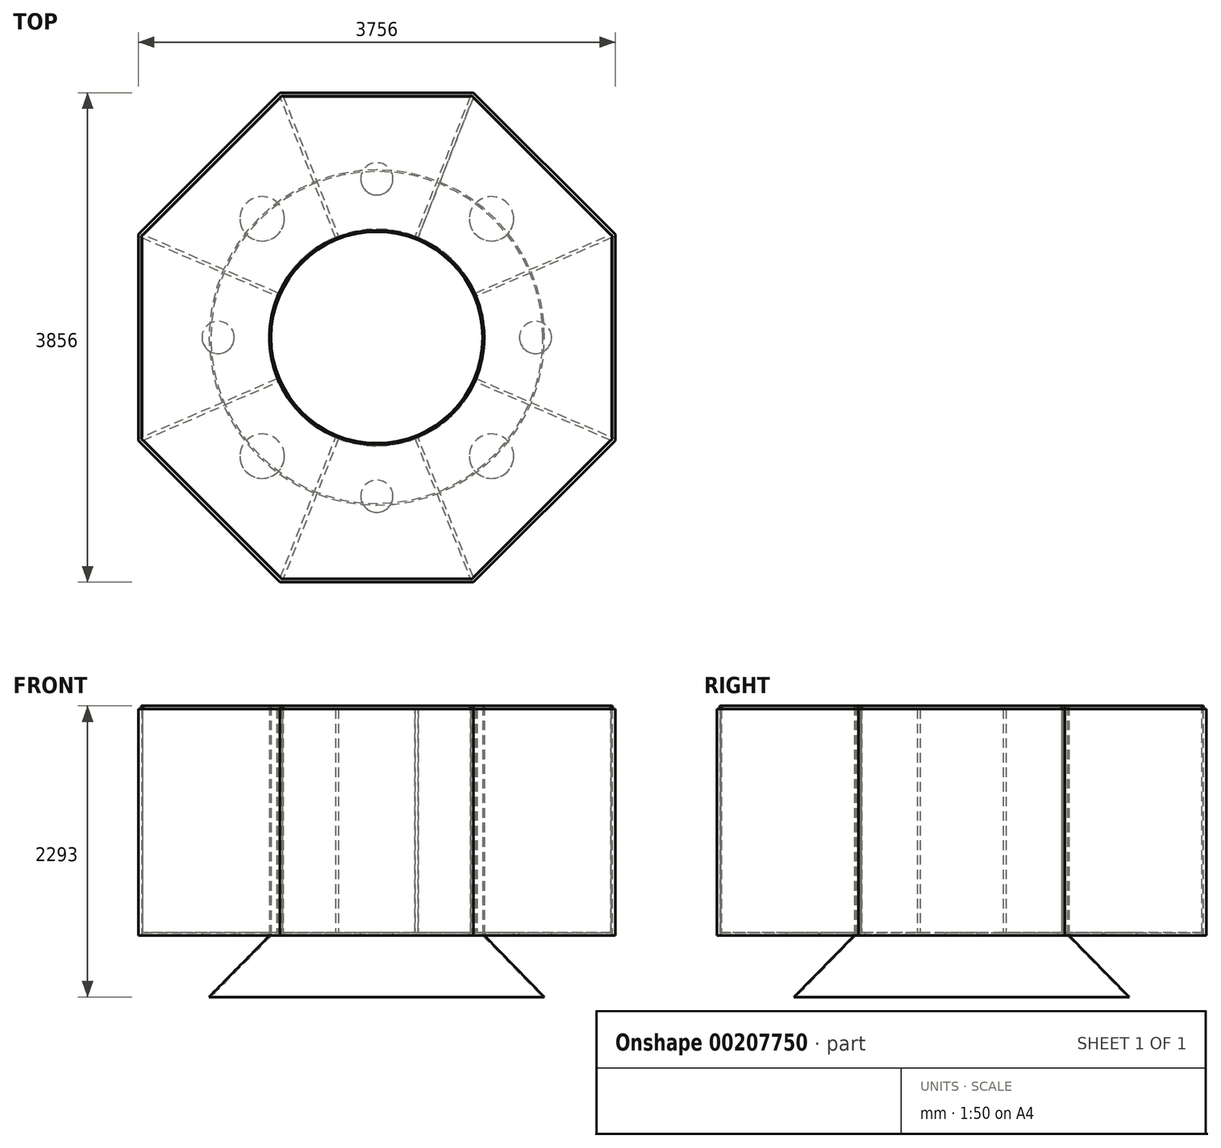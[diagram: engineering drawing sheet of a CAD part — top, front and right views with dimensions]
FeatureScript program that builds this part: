
annotation { "Feature Type Name" : "Feature", "Feature Type Description" : "" }
export const myFeature = defineFeature(function(context is Context, id is Id, definition is map)
    precondition{}
    {
        {
            var Q0;
            Q0=qCreatedBy(makeId("Front.planeOp"),FACE);
            var sketch = newSketch(context, id + "F0", { "sketchPlane" : qUnion([Q0])});
            skLineSegment(sketch, "E0", {"start": v(833, 4071) * mm, "end": v(833, 2261) * mm});
            skLineSegment(sketch, "E1", {"start": v(833, 2261) * mm, "end": v(1308, 1778) * mm});
            skLineSegment(sketch, "E2", {"start": v(1320.7, 1778) * mm, "end": v(845.7, 2261) * mm});
            skLineSegment(sketch, "E3", {"start": v(845.7, 2261) * mm, "end": v(845.7, 4071) * mm});
            skLineSegment(sketch, "E4", {"start": v(845.7, 4071) * mm, "end": v(833, 4071) * mm});
            skLineSegment(sketch, "E5", {"start": v(0, 0) * mm, "end": v(0, 81.95) * mm, "construction": true});
            skLineSegment(sketch, "E6", {"start": v(1308, 1778) * mm, "end": v(1320.7, 1778) * mm});
            skSolve(sketch);
        }
        {
            var Q0;
            Q0 = qSketchRegion(id + "F0", true);
            var Q1;
            Q1=sQuery(id+"F0.wireOp",EDGE,"E5");
            revolve(context, id + "F1", {"surfaceOperationType" : NewSurfaceOperationType.NEW, "entities" : qUnion([Q0]), "axis" : qUnion([Q1]), "revolveType" : RevolveType.FULL});
        }
        {
            var Q0;
            Q0=makeQuery(id+"F1.opRevolve","SWEPT_FACE",FACE,{"disambiguationData":[OSD([sQuery(id+"F0.wireOp",EDGE,"E6")])]});
            cPlane(context, id + "F2", {"entities" : qUnion([Q0]), "cplaneType" : CPlaneType.OFFSET, "offset" : 483 * mm, "oppositeDirection" : true, "width" : 150 * mm, "height" : 150 * mm});
        }
        {
            var Q0;
            Q0=qCreatedBy(id+"F2.planeOp",FACE);
            var sketch = newSketch(context, id + "F3", { "sketchPlane" : qUnion([Q0])});
            skLineSegment(sketch, "E7", {"start": v(-750, -1900) * mm, "end": v(750, -1900) * mm});
            skLineSegment(sketch, "E8", {"start": v(750, -1900) * mm, "end": v(1850, -800) * mm});
            skLineSegment(sketch, "E9", {"start": v(1850, -800) * mm, "end": v(1850, 800) * mm});
            skLineSegment(sketch, "E10", {"start": v(1850, 800) * mm, "end": v(750, 1900) * mm});
            skLineSegment(sketch, "E11", {"start": v(750, 1900) * mm, "end": v(-750, 1900) * mm});
            skLineSegment(sketch, "E12", {"start": v(-750, 1900) * mm, "end": v(-1850, 800) * mm});
            skLineSegment(sketch, "E13", {"start": v(-1850, 800) * mm, "end": v(-1850, -800) * mm});
            skLineSegment(sketch, "E14", {"start": v(-1850, -800) * mm, "end": v(-750, -1900) * mm});
            skCircle(sketch, "E15", {"center": v(0, 0) * mm, "radius": 853.2 * mm});
            skSolve(sketch);
        }
        {
            var Q0;
            Q0 = qSketchRegion(id + "F3", true);
            extrude(context, id + "F4", {"entities" : qUnion([Q0]), "operationType" : NewBodyOperationType.ADD, "oppositeDirection" : true, "depth" : 25 * mm, "offsetDistance" : 25 * mm});
        }
        {
            var Q0;
            Q0=makeQuery(id+"F4.opExtrude","CAP_FACE",FACE,{"disambiguationData":[OSD([sQuery(id+"F3.wireOp",EDGE,"E7"),sQuery(id+"F3.wireOp",EDGE,"E8"),sQuery(id+"F3.wireOp",EDGE,"E9"),sQuery(id+"F3.wireOp",EDGE,"E10"),sQuery(id+"F3.wireOp",EDGE,"E11"),sQuery(id+"F3.wireOp",EDGE,"E12"),sQuery(id+"F3.wireOp",EDGE,"E13"),sQuery(id+"F3.wireOp",EDGE,"E14"),sQuery(id+"F3.wireOp",EDGE,"E15")])],"isStart":false});
            var sketch = newSketch(context, id + "F5", { "sketchPlane" : qUnion([Q0])});
            skCircle(sketch, "E16", {"center": v(0, 1250) * mm, "radius": 127 * mm});
            skCircle(sketch, "E17", {"center": v(-1250, 0) * mm, "radius": 127 * mm});
            skCircle(sketch, "E18", {"center": v(0, -1250) * mm, "radius": 127 * mm});
            skCircle(sketch, "E19", {"center": v(1250, 0) * mm, "radius": 127 * mm});
            skSolve(sketch);
        }
        {
            var Q0;
            Q0 = qSketchRegion(id + "F5", true);
            extrude(context, id + "F6", {"entities" : qUnion([Q0]), "operationType" : NewBodyOperationType.REMOVE, "endBound" : BoundingType.UP_TO_NEXT, "oppositeDirection" : true, "depth" : 25 * mm, "offsetDistance" : 25 * mm});
        }
        {
            var Q0;
            Q0=makeQuery(id+"F4.opExtrude","CAP_FACE",FACE,{"disambiguationData":[OSD([sQuery(id+"F3.wireOp",EDGE,"E7"),sQuery(id+"F3.wireOp",EDGE,"E8"),sQuery(id+"F3.wireOp",EDGE,"E9"),sQuery(id+"F3.wireOp",EDGE,"E10"),sQuery(id+"F3.wireOp",EDGE,"E11"),sQuery(id+"F3.wireOp",EDGE,"E12"),sQuery(id+"F3.wireOp",EDGE,"E13"),sQuery(id+"F3.wireOp",EDGE,"E14"),sQuery(id+"F3.wireOp",EDGE,"E15")])],"isStart":false});
            var sketch = newSketch(context, id + "F7", { "sketchPlane" : qUnion([Q0])});
            skCircle(sketch, "E20", {"center": v(-903.06, 935.14) * mm, "radius": 175 * mm});
            skCircle(sketch, "E21", {"center": v(903.06, 935.14) * mm, "radius": 175 * mm});
            skCircle(sketch, "E22", {"center": v(-903.06, -935.14) * mm, "radius": 175 * mm});
            skCircle(sketch, "E23", {"center": v(903.06, -935.14) * mm, "radius": 175 * mm});
            skLineSegment(sketch, "E24", {"start": v(0, 0) * mm, "end": v(-903.06, 935.14) * mm, "construction": true});
            skCircle(sketch, "E25", {"center": v(0, 0) * mm, "radius": 1300 * mm, "construction": true});
            skSolve(sketch);
        }
        {
            var Q0;
            Q0 = qSketchRegion(id + "F7", true);
            extrude(context, id + "F8", {"entities" : qUnion([Q0]), "operationType" : NewBodyOperationType.REMOVE, "endBound" : BoundingType.UP_TO_NEXT, "oppositeDirection" : true, "depth" : 25 * mm, "offsetDistance" : 25 * mm});
        }
        {
            var Q0;
            Q0=qCreatedBy(makeId("Right.planeOp"),FACE);
            var sketch = newSketch(context, id + "F9", { "sketchPlane" : qUnion([Q0])});
            skLineSegment(sketch, "E26", {"start": v(0, 0) * mm, "end": v(0, 400.79) * mm, "construction": true});
            skSolve(sketch);
        }
        {
            var Q0;
            Q0=makeQuery(id+"F4.opExtrude","CAP_FACE",FACE,{"disambiguationData":[OSD([sQuery(id+"F3.wireOp",EDGE,"E7"),sQuery(id+"F3.wireOp",EDGE,"E8"),sQuery(id+"F3.wireOp",EDGE,"E9"),sQuery(id+"F3.wireOp",EDGE,"E10"),sQuery(id+"F3.wireOp",EDGE,"E11"),sQuery(id+"F3.wireOp",EDGE,"E12"),sQuery(id+"F3.wireOp",EDGE,"E13"),sQuery(id+"F3.wireOp",EDGE,"E14"),sQuery(id+"F3.wireOp",EDGE,"E15")])],"isStart":false});
            var sketch = newSketch(context, id + "F10", { "sketchPlane" : qUnion([Q0])});
            skLineSegment(sketch, "E27", {"start": v(-1850, 800) * mm, "end": v(0, 0) * mm, "construction": true});
            skLineSegment(sketch, "E28", {"start": v(-750, 1900) * mm, "end": v(0, 0) * mm, "construction": true});
            skLineSegment(sketch, "E29", {"start": v(0, 0) * mm, "end": v(750, 1900) * mm, "construction": true});
            skLineSegment(sketch, "E30", {"start": v(0, 0) * mm, "end": v(1850, 800) * mm, "construction": true});
            skLineSegment(sketch, "E31", {"start": v(-1845.04, 811.47) * mm, "end": v(-778.07, 350.08) * mm});
            skLineSegment(sketch, "E32", {"start": v(-778.07, 350.08) * mm, "end": v(-788, 327.14) * mm});
            skLineSegment(sketch, "E33", {"start": v(-788, 327.14) * mm, "end": v(-1854.96, 788.53) * mm});
            skLineSegment(sketch, "E34", {"start": v(-738.37, 1904.59) * mm, "end": v(-761.58, 1895.29) * mm});
            skLineSegment(sketch, "E35", {"start": v(-761.58, 1895.29) * mm, "end": v(-324.86, 788.93) * mm});
            skLineSegment(sketch, "E36", {"start": v(-301.6, 798.11) * mm, "end": v(-324.86, 788.93) * mm});
            skLineSegment(sketch, "E37", {"start": v(-301.6, 798.11) * mm, "end": v(-738.37, 1904.59) * mm});
            skLineSegment(sketch, "E38", {"start": v(738.37, 1904.59) * mm, "end": v(761.63, 1895.41) * mm});
            skLineSegment(sketch, "E39", {"start": v(761.63, 1895.41) * mm, "end": v(324.86, 788.93) * mm});
            skLineSegment(sketch, "E40", {"start": v(301.6, 798.11) * mm, "end": v(738.37, 1904.59) * mm});
            skLineSegment(sketch, "E41", {"start": v(1845.04, 811.47) * mm, "end": v(778.07, 350.08) * mm});
            skLineSegment(sketch, "E42", {"start": v(788, 327.14) * mm, "end": v(778.07, 350.08) * mm});
            skLineSegment(sketch, "E43", {"start": v(788, 327.14) * mm, "end": v(1854.96, 788.53) * mm});
            skLineSegment(sketch, "E44", {"start": v(-1854.96, -788.53) * mm, "end": v(-1845.04, -811.47) * mm});
            skLineSegment(sketch, "E45", {"start": v(-1854.96, -788.53) * mm, "end": v(-788, -327.14) * mm});
            skLineSegment(sketch, "E46", {"start": v(-778.07, -350.08) * mm, "end": v(-788, -327.14) * mm});
            skLineSegment(sketch, "E47", {"start": v(-778.07, -350.08) * mm, "end": v(-1845.04, -811.47) * mm});
            skLineSegment(sketch, "E48", {"start": v(-761.33, -1894.66) * mm, "end": v(-738.37, -1904.59) * mm});
            skLineSegment(sketch, "E49", {"start": v(-738.37, -1904.59) * mm, "end": v(-301.6, -798.11) * mm});
            skLineSegment(sketch, "E50", {"start": v(-301.6, -798.11) * mm, "end": v(-324.86, -788.93) * mm});
            skLineSegment(sketch, "E51", {"start": v(-324.86, -788.93) * mm, "end": v(-761.33, -1894.66) * mm});
            skLineSegment(sketch, "E52", {"start": v(761.32, -1894.65) * mm, "end": v(738.37, -1904.57) * mm});
            skLineSegment(sketch, "E53", {"start": v(738.37, -1904.57) * mm, "end": v(301.61, -798.11) * mm});
            skLineSegment(sketch, "E54", {"start": v(301.61, -798.11) * mm, "end": v(324.85, -788.94) * mm});
            skLineSegment(sketch, "E55", {"start": v(324.85, -788.94) * mm, "end": v(761.32, -1894.65) * mm});
            skLineSegment(sketch, "E56", {"start": v(1854.59, -788.37) * mm, "end": v(1845.41, -811.63) * mm});
            skLineSegment(sketch, "E57", {"start": v(1854.59, -788.37) * mm, "end": v(788, -327.14) * mm});
            skLineSegment(sketch, "E58", {"start": v(788, -327.14) * mm, "end": v(778.07, -350.08) * mm});
            skLineSegment(sketch, "E59", {"start": v(778.07, -350.08) * mm, "end": v(1845.41, -811.63) * mm});
            skLineSegment(sketch, "E60", {"start": v(-1854.96, 788.53) * mm, "end": v(-1845.04, 811.47) * mm});
            skLineSegment(sketch, "E61", {"start": v(1845.04, 811.47) * mm, "end": v(1854.96, 788.53) * mm});
            skLineSegment(sketch, "E62", {"start": v(301.6, 798.11) * mm, "end": v(324.86, 788.93) * mm});
            skSolve(sketch);
        }
        {
            var Q0;
            Q0 = qSketchRegion(id + "F10", true);
            var Q1;
            Q1=makeQuery(id+"F1.opRevolve","SWEPT_FACE",FACE,{"disambiguationData":[OSD([sQuery(id+"F0.wireOp",EDGE,"E4")])]});
            extrude(context, id + "F11", {"entities" : qUnion([Q0]), "operationType" : NewBodyOperationType.ADD, "endBound" : BoundingType.UP_TO_SURFACE, "depth" : 25 * mm, "endBoundEntityFace" : qUnion([Q1]), "offsetDistance" : 25 * mm});
        }
        {
            var Q0;
            Q0=makeQuery(id+"F1.opRevolve","SWEPT_FACE",FACE,{"disambiguationData":[OSD([sQuery(id+"F0.wireOp",EDGE,"E4")])]});
            var sketch = newSketch(context, id + "F12", { "sketchPlane" : qUnion([Q0])});
            skPoint(sketch, "E63.0.end.orphan", {"position": v(-750.12, 1899.88) * mm});
            skPoint(sketch, "E63.0.start.orphan", {"position": v(-750.12, 1899.88) * mm});
            skPoint(sketch, "E64.0.end.orphan", {"position": v(-1850, -786.38) * mm});
            skPoint(sketch, "E64.0.start.orphan", {"position": v(-1850, -800) * mm});
            skLineSegment(sketch, "E65.0", {"start": v(-1850, 800) * mm, "end": v(-750, 1900) * mm});
            skLineSegment(sketch, "E66.0", {"start": v(-750, 1900) * mm, "end": v(750, 1900) * mm});
            skLineSegment(sketch, "E67.0", {"start": v(-1850, -800) * mm, "end": v(-1850, 800) * mm});
            skLineSegment(sketch, "E68.0", {"start": v(-750, -1900) * mm, "end": v(-1850, -800) * mm});
            skLineSegment(sketch, "E69.0", {"start": v(750, -1900) * mm, "end": v(-750, -1900) * mm});
            skLineSegment(sketch, "E70.0", {"start": v(1850, -800) * mm, "end": v(750, -1900) * mm});
            skLineSegment(sketch, "E71.0", {"start": v(1850, 800) * mm, "end": v(1850, -800) * mm});
            skLineSegment(sketch, "E72.0", {"start": v(750, 1900) * mm, "end": v(1850, 800) * mm});
            skCircle(sketch, "E73.0", {"center": v(0, 0) * mm, "radius": 845.7 * mm});
            skSolve(sketch);
        }
        {
            var Q0;
            Q0 = qSketchRegion(id + "F12", true);
            extrude(context, id + "F13", {"entities" : qUnion([Q0]), "oppositeDirection" : true, "depth" : 25 * mm, "offsetDistance" : 25 * mm});
        }
        {
            var Q0;
            Q0=makeQuery(id+"F13.opExtrude","SWEPT_BODY",BODY,{"disambiguationData":[OSD([sQuery(id+"F12.wireOp",EDGE,"E65.0"),sQuery(id+"F12.wireOp",EDGE,"E66.0"),sQuery(id+"F12.wireOp",EDGE,"E67.0"),sQuery(id+"F12.wireOp",EDGE,"E68.0"),sQuery(id+"F12.wireOp",EDGE,"E69.0"),sQuery(id+"F12.wireOp",EDGE,"E70.0"),sQuery(id+"F12.wireOp",EDGE,"E71.0"),sQuery(id+"F12.wireOp",EDGE,"E72.0"),sQuery(id+"F12.wireOp",EDGE,"E73.0")])]});
            var Q1;
            Q1=makeQuery(id+"F4.opExtrude","SWEPT_BODY",BODY,{"disambiguationData":[OSD([sQuery(id+"F3.wireOp",EDGE,"E7"),sQuery(id+"F3.wireOp",EDGE,"E8"),sQuery(id+"F3.wireOp",EDGE,"E9"),sQuery(id+"F3.wireOp",EDGE,"E10"),sQuery(id+"F3.wireOp",EDGE,"E11"),sQuery(id+"F3.wireOp",EDGE,"E12"),sQuery(id+"F3.wireOp",EDGE,"E13"),sQuery(id+"F3.wireOp",EDGE,"E14"),sQuery(id+"F3.wireOp",EDGE,"E15")])]});
            booleanBodies(context, id + "F14", {"operationType" : BooleanOperationType.UNION, "tools" : qUnion([Q0, Q1])});
        }
        {
            var Q0;
            Q0=makeQuery(id+"F4.opExtrude","CAP_FACE",FACE,{"disambiguationData":[OSD([sQuery(id+"F3.wireOp",EDGE,"E7"),sQuery(id+"F3.wireOp",EDGE,"E8"),sQuery(id+"F3.wireOp",EDGE,"E9"),sQuery(id+"F3.wireOp",EDGE,"E10"),sQuery(id+"F3.wireOp",EDGE,"E11"),sQuery(id+"F3.wireOp",EDGE,"E12"),sQuery(id+"F3.wireOp",EDGE,"E13"),sQuery(id+"F3.wireOp",EDGE,"E14"),sQuery(id+"F3.wireOp",EDGE,"E15")])],"isStart":true});
            var sketch = newSketch(context, id + "F15", { "sketchPlane" : qUnion([Q0])});
            skLineSegment(sketch, "E74.0", {"start": v(751.24, -1903) * mm, "end": v(1853, -801.24) * mm});
            skLineSegment(sketch, "E74.1", {"start": v(-751.24, -1903) * mm, "end": v(751.24, -1903) * mm});
            skLineSegment(sketch, "E74.2", {"start": v(1853, -801.24) * mm, "end": v(1853, 801.24) * mm});
            skLineSegment(sketch, "E74.3", {"start": v(-1853, -801.24) * mm, "end": v(-751.24, -1903) * mm});
            skLineSegment(sketch, "E74.4", {"start": v(1853, 801.24) * mm, "end": v(751.24, 1903) * mm});
            skLineSegment(sketch, "E74.5", {"start": v(751.24, 1903) * mm, "end": v(-751.24, 1903) * mm});
            skLineSegment(sketch, "E74.6", {"start": v(-751.24, 1903) * mm, "end": v(-1853, 801.24) * mm});
            skLineSegment(sketch, "E74.7", {"start": v(-1853, 801.24) * mm, "end": v(-1853, -801.24) * mm});
            skLineSegment(sketch, "E75.0", {"start": v(761.6, -1928) * mm, "end": v(1878, -811.6) * mm});
            skLineSegment(sketch, "E75.1", {"start": v(-761.6, -1928) * mm, "end": v(761.6, -1928) * mm});
            skLineSegment(sketch, "E75.2", {"start": v(1878, -811.6) * mm, "end": v(1878, 811.6) * mm});
            skLineSegment(sketch, "E75.3", {"start": v(-1878, -811.6) * mm, "end": v(-761.6, -1928) * mm});
            skLineSegment(sketch, "E75.4", {"start": v(1878, 811.6) * mm, "end": v(761.6, 1928) * mm});
            skLineSegment(sketch, "E75.5", {"start": v(761.6, 1928) * mm, "end": v(-761.6, 1928) * mm});
            skLineSegment(sketch, "E75.6", {"start": v(-761.6, 1928) * mm, "end": v(-1878, 811.6) * mm});
            skLineSegment(sketch, "E75.7", {"start": v(-1878, 811.6) * mm, "end": v(-1878, -811.6) * mm});
            skSolve(sketch);
        }
        {
            var Q0;
            Q0 = qSketchRegion(id + "F15", true);
            var Q1;
            {var subQ0=sQuery(id+"F12.wireOp",EDGE,"E72.0");var subQ1=sQuery(id+"F12.wireOp",EDGE,"E71.0");var subQ2=sQuery(id+"F12.wireOp",EDGE,"E66.0");var subQ3=sQuery(id+"F12.wireOp",EDGE,"E67.0");var subQ4=sQuery(id+"F12.wireOp",EDGE,"E73.0");var subQ5=sQuery(id+"F12.wireOp",EDGE,"E65.0");var subQ6=sQuery(id+"F12.wireOp",EDGE,"E68.0");var subQ7=sQuery(id+"F12.wireOp",EDGE,"E69.0");var subQ8=sQuery(id+"F12.wireOp",EDGE,"E70.0");Q1=makeQuery(id+"F14.opBoolean","SPLIT",FACE,{"disambiguationData":[TD([makeQuery(id+"F11.opExtrude","SWEPT_FACE",FACE,{"disambiguationData":[OSD([sQuery(id+"F10.wireOp",EDGE,"E31")])]})])],"derivedFrom":makeQuery(id+"F13.opExtrude","CAP_FACE",FACE,{"disambiguationData":[OSD([subQ5,subQ2,subQ3,subQ6,subQ7,subQ8,subQ1,subQ0,subQ4])],"isStart":false})});}
            extrude(context, id + "F16", {"entities" : qUnion([Q0]), "operationType" : NewBodyOperationType.ADD, "endBound" : BoundingType.UP_TO_SURFACE, "oppositeDirection" : true, "depth" : 25 * mm, "endBoundEntityFace" : qUnion([Q1]), "offsetDistance" : 25 * mm});
        }
    });
